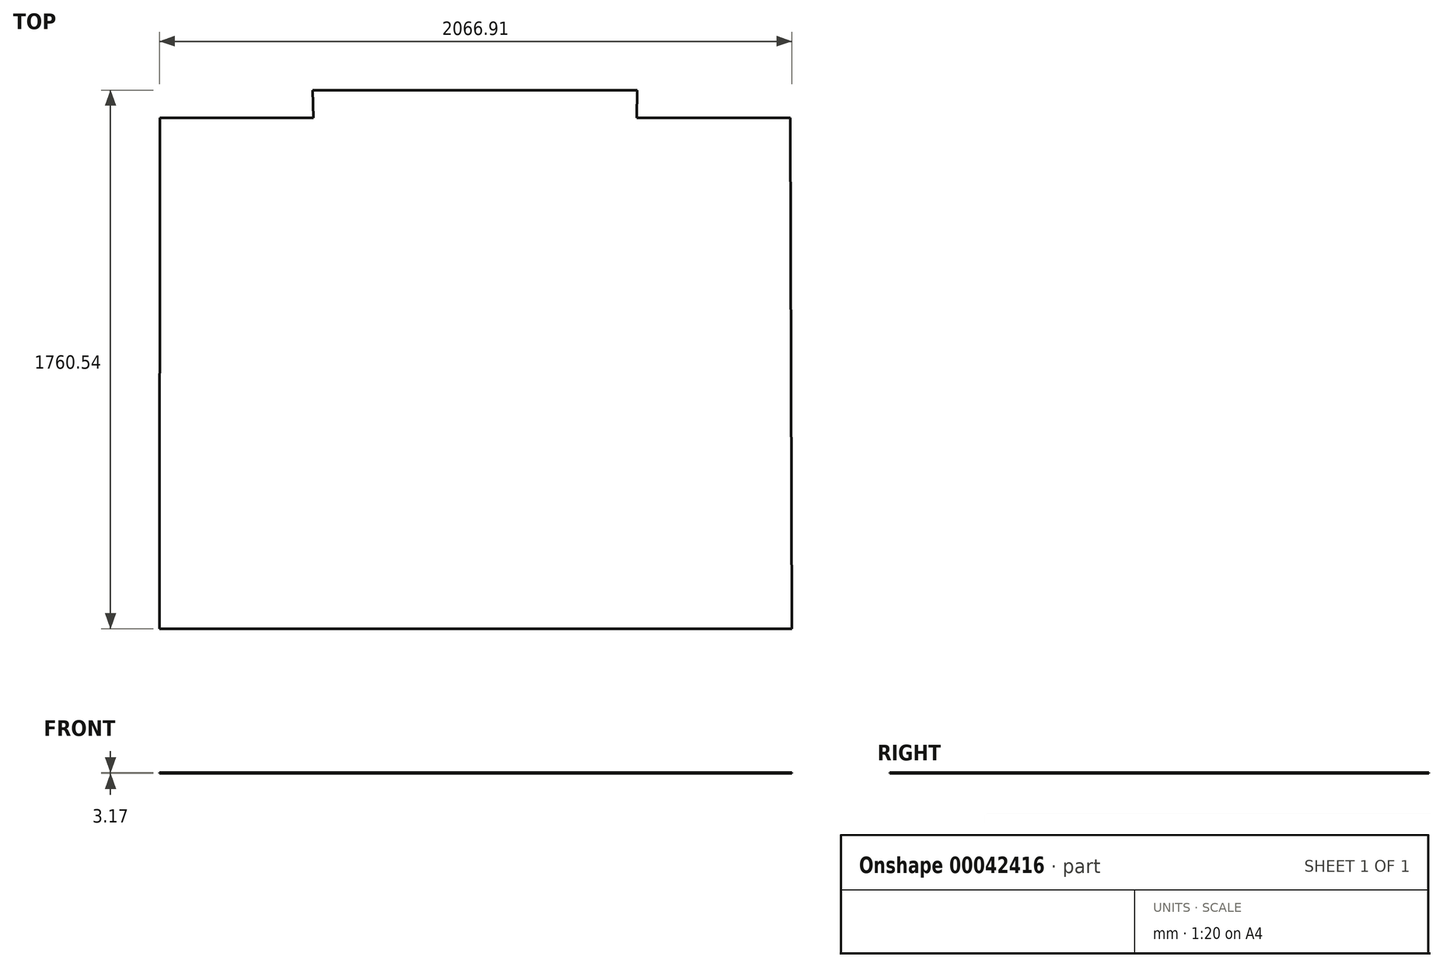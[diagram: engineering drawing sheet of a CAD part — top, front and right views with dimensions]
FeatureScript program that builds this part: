
annotation { "Feature Type Name" : "Feature", "Feature Type Description" : "" }
export const myFeature = defineFeature(function(context is Context, id is Id, definition is map)
    precondition{}
    {
        {
            var Q0;
            Q0=qCreatedBy(makeId("Top.planeOp"),FACE);
            var sketch = newSketch(context, id + "F0", { "sketchPlane" : qUnion([Q0])});
            skLineSegment(sketch, "E0", {"start": v(-531.81, 881.86) * mm, "end": v(531.81, 881.86) * mm});
            skLineSegment(sketch, "E1", {"start": v(1031.58, 791.36) * mm, "end": v(1037.1, -881.86) * mm});
            skPoint(sketch, "E2", {"position": v(1034.2, 0) * mm});
            skLineSegment(sketch, "E3", {"start": v(-1031.57, 791.37) * mm, "end": v(-1033, -881.86) * mm});
            skPoint(sketch, "E4", {"position": v(-1032.25, 0) * mm});
            skLineSegment(sketch, "E5", {"start": v(-1031.57, 791.37) * mm, "end": v(-529.92, 791.39) * mm});
            skLineSegment(sketch, "E6", {"start": v(-529.92, 791.39) * mm, "end": v(-531.81, 881.86) * mm});
            skLineSegment(sketch, "E7", {"start": v(531.81, 881.86) * mm, "end": v(529.93, 791.39) * mm});
            skLineSegment(sketch, "E8", {"start": v(529.93, 791.39) * mm, "end": v(1031.58, 791.36) * mm});
            skPoint(sketch, "E9", {"position": v(0, 881.86) * mm});
            skPoint(sketch, "E10", {"position": v(0, -881.86) * mm});
            skLineSegment(sketch, "E11", {"start": v(0, 881.86) * mm, "end": v(0, -881.86) * mm, "construction": true});
            skPoint(sketch, "E12", {"position": v(0, 0) * mm});
            skLineSegment(sketch, "E13", {"start": v(-1033, -881.86) * mm, "end": v(1037.1, -881.86) * mm});
            skSolve(sketch);
        }
        {
            var Q0;
            Q0=qCreatedBy(makeId("Top.planeOp"),FACE);
            var sketch = newSketch(context, id + "F1", { "sketchPlane" : qUnion([Q0])});
            skLineSegment(sketch, "E14.0", {"start": v(528.31, 789.8) * mm, "end": v(530.2, 880.27) * mm});
            skLineSegment(sketch, "E14.1", {"start": v(1030, 789.77) * mm, "end": v(528.31, 789.8) * mm});
            skLineSegment(sketch, "E14.2", {"start": v(530.2, 880.27) * mm, "end": v(-530.2, 880.27) * mm});
            skLineSegment(sketch, "E14.3", {"start": v(1035.5, -880.27) * mm, "end": v(1030, 789.77) * mm});
            skLineSegment(sketch, "E14.4", {"start": v(-530.2, 880.27) * mm, "end": v(-528.3, 789.8) * mm});
            skLineSegment(sketch, "E14.5", {"start": v(-528.3, 789.8) * mm, "end": v(-1029.98, 789.78) * mm});
            skLineSegment(sketch, "E14.6", {"start": v(-1029.98, 789.78) * mm, "end": v(-1031.41, -880.27) * mm});
            skLineSegment(sketch, "E14.7", {"start": v(-1031.41, -880.27) * mm, "end": v(1035.5, -880.27) * mm});
            skSolve(sketch);
        }
        {
            var Q0;
            Q0=qSketchRegion(id+"F1",true);
            extrude(context, id + "F2", {"entities" : qUnion([Q0]), "depth" : 3.17 * mm});
        }
    });
